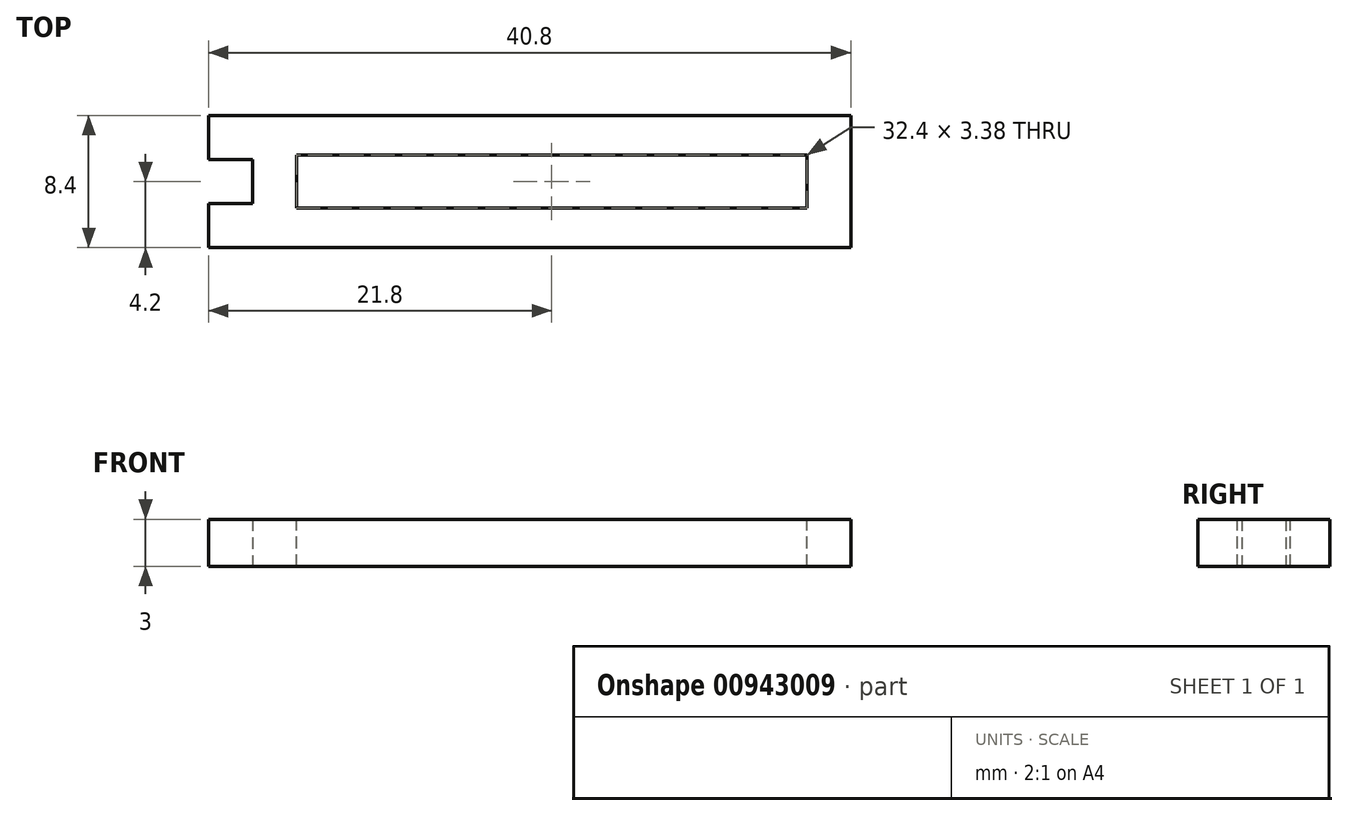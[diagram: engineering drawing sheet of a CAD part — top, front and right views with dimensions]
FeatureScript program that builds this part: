
annotation { "Feature Type Name" : "Feature", "Feature Type Description" : "" }
export const myFeature = defineFeature(function(context is Context, id is Id, definition is map)
    precondition{}
    {
        {
            var Q0;
            Q0=qCreatedBy(makeId("Top.planeOp"),FACE);
            var sketch = newSketch(context, id + "F0", { "sketchPlane" : qUnion([Q0])});
            skLineSegment(sketch, "E0.bottom", {"start": v(19, 4.2) * mm, "end": v(-19, 4.2) * mm});
            skLineSegment(sketch, "E0.top", {"start": v(19, -4.2) * mm, "end": v(-19, -4.2) * mm});
            skLineSegment(sketch, "E0.left", {"start": v(19, 4.2) * mm, "end": v(19, -4.2) * mm});
            skLineSegment(sketch, "E0.right", {"start": v(-19, 4.2) * mm, "end": v(-19, -4.2) * mm});
            skPoint(sketch, "E0.middle", {"position": v(0, 0) * mm});
            skSolve(sketch);
        }
        {
            var Q0;
            Q0 = qSketchRegion(id + "F0", true);
            extrude(context, id + "F1", {"entities" : qUnion([Q0]), "depth" : 3 * mm, "offsetDistance" : 25 * mm});
        }
        {
            var Q0;
            Q0=makeQuery(id+"F1.opExtrude","SWEPT_FACE",FACE,{"disambiguationData":[OSD([sQuery(id+"F0.wireOp",EDGE,"E0.right")])]});
            var sketch = newSketch(context, id + "F2", { "sketchPlane" : qUnion([Q0])});
            skLineSegment(sketch, "E1", {"start": v(-1.4, 3) * mm, "end": v(-1.4, 0) * mm});
            skLineSegment(sketch, "E2", {"start": v(1.4, 3) * mm, "end": v(1.4, 0) * mm});
            skSolve(sketch);
        }
        {
            var Q0;
            {var subQ0=sQuery(id+"F2.wireOp",EDGE,"E1");Q0=makeQuery(id+"F2.imprint","IMPRINT",FACE,{"disambiguationData":[TD([[makeQuery(id+"F2.imprint","IMPRINT",EDGE,{"derivedFrom":subQ0}),-1.0]])]});}
            var Q1;
            {var subQ0=sQuery(id+"F2.wireOp",EDGE,"E2");Q1=makeQuery(id+"F2.imprint","IMPRINT",FACE,{"disambiguationData":[TD([[makeQuery(id+"F2.imprint","IMPRINT",EDGE,{"derivedFrom":subQ0}),1.0]])]});}
            extrude(context, id + "F3", {"entities" : qUnion([Q0, Q1]), "operationType" : NewBodyOperationType.ADD, "depth" : 2.8 * mm, "offsetDistance" : 25 * mm});
        }
        {
            var Q0;
            Q0=makeQuery(id+"F1.opExtrude","CAP_FACE",FACE,{"disambiguationData":[OSD([sQuery(id+"F0.wireOp",EDGE,"E0.bottom"),sQuery(id+"F0.wireOp",EDGE,"E0.top"),sQuery(id+"F0.wireOp",EDGE,"E0.left"),sQuery(id+"F0.wireOp",EDGE,"E0.right")])],"isStart":false});
            var sketch = newSketch(context, id + "F4", { "sketchPlane" : qUnion([Q0])});
            skLineSegment(sketch, "E3.bottom", {"start": v(16.2, 1.7) * mm, "end": v(-16.2, 1.7) * mm});
            skLineSegment(sketch, "E3.top", {"start": v(16.2, -1.7) * mm, "end": v(-16.2, -1.7) * mm});
            skLineSegment(sketch, "E3.left", {"start": v(16.2, 1.7) * mm, "end": v(16.2, -1.7) * mm});
            skLineSegment(sketch, "E3.right", {"start": v(-16.2, 1.7) * mm, "end": v(-16.2, -1.7) * mm});
            skPoint(sketch, "E3.middle", {"position": v(0, 0) * mm});
            skSolve(sketch);
        }
        {
            var Q0;
            Q0=makeQuery(id+"F4.imprint","IMPRINT",FACE,{"disambiguationData":[TD([[makeQuery(id+"F4.imprint","IMPRINT",EDGE,{"derivedFrom":sQuery(id+"F4.wireOp",EDGE,"E3.bottom")}),1.0]])]});
            extrude(context, id + "F5", {"entities" : qUnion([Q0]), "operationType" : NewBodyOperationType.REMOVE, "oppositeDirection" : true, "depth" : 25 * mm, "offsetDistance" : 25 * mm});
        }
    });
